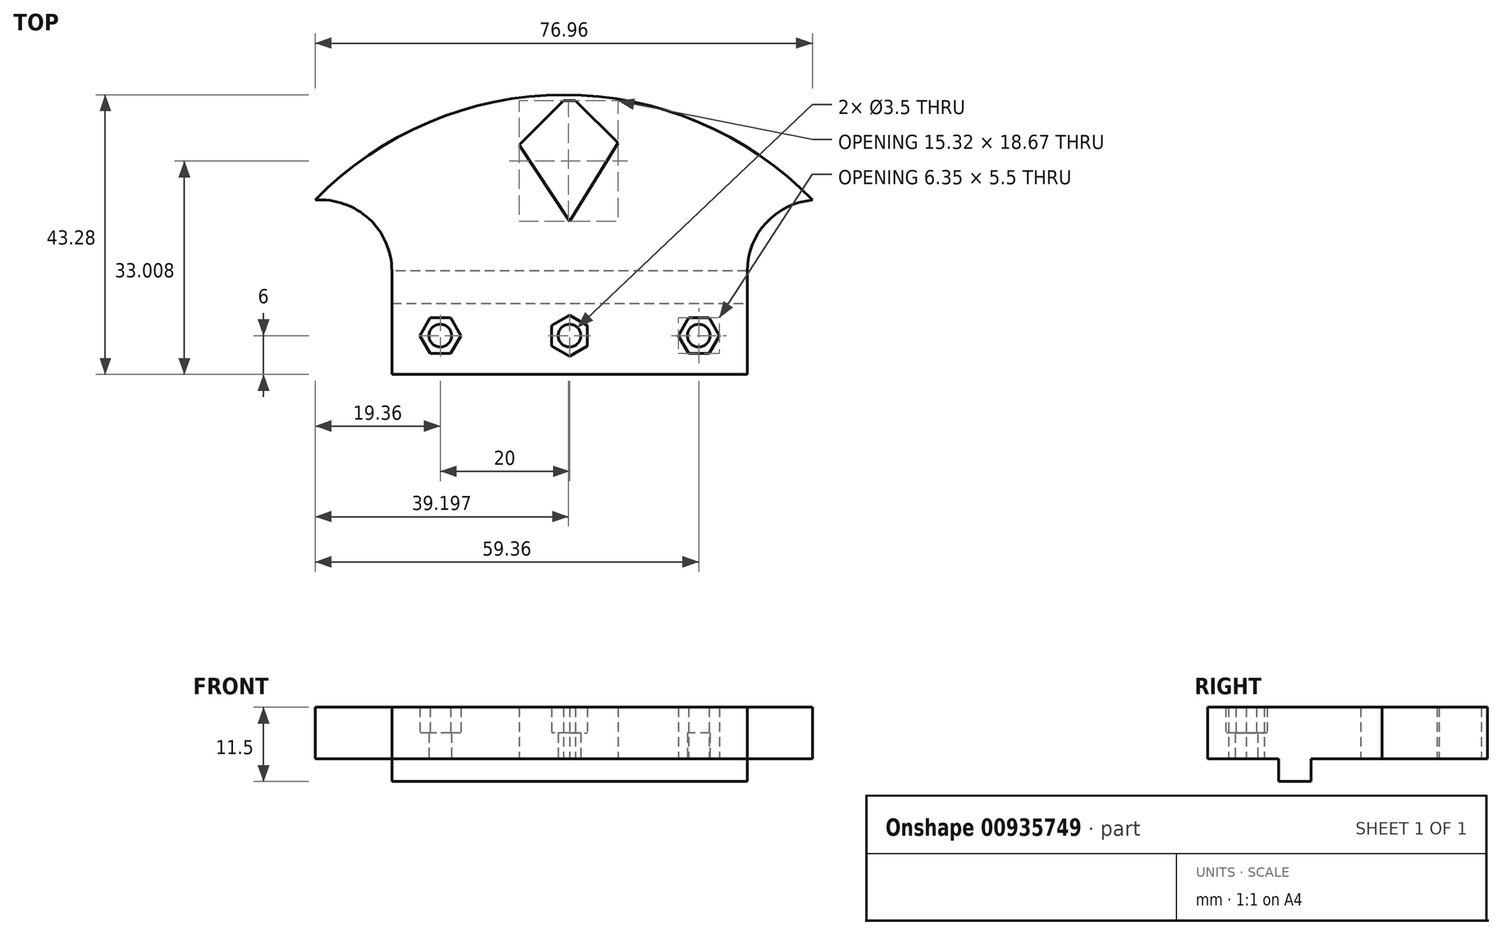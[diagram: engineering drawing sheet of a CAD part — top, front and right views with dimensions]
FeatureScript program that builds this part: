
annotation { "Feature Type Name" : "Feature", "Feature Type Description" : "" }
export const myFeature = defineFeature(function(context is Context, id is Id, definition is map)
    precondition{}
    {
        {
            var Q0;
            Q0=qCreatedBy(makeId("Top.planeOp"),FACE);
            var sketch = newSketch(context, id + "F0", { "sketchPlane" : qUnion([Q0])});
            skLineSegment(sketch, "E0.bottom", {"start": v(27.5, 8) * mm, "end": v(-27.5, 8) * mm});
            skLineSegment(sketch, "E0.top", {"start": v(27.5, -8) * mm, "end": v(-27.5, -8) * mm});
            skLineSegment(sketch, "E0.left", {"start": v(27.5, 8) * mm, "end": v(27.5, -8) * mm});
            skLineSegment(sketch, "E0.right", {"start": v(-27.5, 8) * mm, "end": v(-27.5, -8) * mm});
            skPoint(sketch, "E0.middle", {"position": v(0, 0) * mm});
            skLineSegment(sketch, "E1", {"start": v(-27.5, 3) * mm, "end": v(27.5, 3) * mm});
            skCircle(sketch, "E2.cCircle", {"center": v(0, -2) * mm, "radius": 2.75 * mm, "construction": true});
            skLineSegment(sketch, "E2.0", {"start": v(2.75, -0.41) * mm, "end": v(2.75, -3.59) * mm});
            skLineSegment(sketch, "E2.1", {"start": v(2.75, -3.59) * mm, "end": v(0, -5.18) * mm});
            skLineSegment(sketch, "E2.2", {"start": v(0, -5.18) * mm, "end": v(-2.75, -3.59) * mm});
            skLineSegment(sketch, "E2.3", {"start": v(-2.75, -3.59) * mm, "end": v(-2.75, -0.41) * mm});
            skLineSegment(sketch, "E2.4", {"start": v(-2.75, -0.41) * mm, "end": v(0, 1.18) * mm});
            skLineSegment(sketch, "E2.5", {"start": v(0, 1.18) * mm, "end": v(2.75, -0.41) * mm});
            skPoint(sketch, "E2.0.midPoint", {"position": v(2.75, -2) * mm});
            skCircle(sketch, "E3", {"center": v(0, -2) * mm, "radius": 1.75 * mm});
            skCircle(sketch, "E4.cCircle", {"center": v(-20, -2) * mm, "radius": 2.75 * mm, "construction": true});
            skLineSegment(sketch, "E4.0", {"start": v(-18.41, -4.75) * mm, "end": v(-21.59, -4.75) * mm});
            skLineSegment(sketch, "E4.1", {"start": v(-21.59, -4.75) * mm, "end": v(-23.18, -2) * mm});
            skLineSegment(sketch, "E4.2", {"start": v(-23.18, -2) * mm, "end": v(-21.59, 0.75) * mm});
            skLineSegment(sketch, "E4.3", {"start": v(-21.59, 0.75) * mm, "end": v(-18.41, 0.75) * mm});
            skLineSegment(sketch, "E4.4", {"start": v(-18.41, 0.75) * mm, "end": v(-16.82, -2) * mm});
            skLineSegment(sketch, "E4.5", {"start": v(-16.82, -2) * mm, "end": v(-18.41, -4.75) * mm});
            skPoint(sketch, "E4.0.midPoint", {"position": v(-20, -4.75) * mm});
            skCircle(sketch, "E5", {"center": v(-20, -2) * mm, "radius": 1.75 * mm});
            skLineSegment(sketch, "E6.MirrorCS", {"start": v(16.82, -2) * mm, "end": v(18.41, -4.75) * mm});
            skCircle(sketch, "E7.MirrorC", {"center": v(20, -2) * mm, "radius": 1.75 * mm});
            skPoint(sketch, "E8.MirrorP", {"position": v(20, -4.75) * mm});
            skLineSegment(sketch, "E9.MirrorCS", {"start": v(18.41, -4.75) * mm, "end": v(21.59, -4.75) * mm});
            skLineSegment(sketch, "E10.MirrorCS", {"start": v(21.59, 0.75) * mm, "end": v(18.41, 0.75) * mm});
            skCircle(sketch, "E11.MirrorC", {"center": v(20, -2) * mm, "radius": 2.75 * mm, "construction": true});
            skLineSegment(sketch, "E12.MirrorCS", {"start": v(18.41, 0.75) * mm, "end": v(16.82, -2) * mm});
            skLineSegment(sketch, "E13.MirrorCS", {"start": v(21.59, -4.75) * mm, "end": v(23.18, -2) * mm});
            skLineSegment(sketch, "E14.MirrorCS", {"start": v(23.18, -2) * mm, "end": v(21.59, 0.75) * mm});
            skArc(sketch, "E15", {"start": v(-27.5, 8) * mm, "mid": v(-31.03, 16.08) * mm, "end": v(-39.36, 18.98) * mm});
            skArc(sketch, "E16", {"start": v(37.6, 18.98) * mm, "mid": v(30.4, 15.46) * mm, "end": v(27.5, 8) * mm});
            skArc(sketch, "E17", {"start": v(37.6, 18.98) * mm, "mid": v(-0.88, 35.28) * mm, "end": v(-39.36, 18.98) * mm});
            skLineSegment(sketch, "E18", {"start": v(-27.5, 8) * mm, "end": v(-0.93, 34.34) * mm});
            skLineSegment(sketch, "E19", {"start": v(0.93, 34.34) * mm, "end": v(27.5, 8) * mm});
            skLineSegment(sketch, "E20", {"start": v(-7.82, 27.51) * mm, "end": v(0, 15.67) * mm});
            skLineSegment(sketch, "E21", {"start": v(0, 15.67) * mm, "end": v(7.5, 27.83) * mm});
            skLineSegment(sketch, "E22", {"start": v(-0.93, 34.34) * mm, "end": v(0.93, 34.34) * mm});
            skPoint(sketch, "E23.orphan", {"position": v(0, 35.27) * mm});
            skSolve(sketch);
        }
        {
            var Q0;
            {var subQ0=sQuery(id+"F0.wireOp",EDGE,"E0.top");Q0=makeQuery(id+"F0.imprint","IMPRINT",FACE,{"disambiguationData":[TD([[makeQuery(id+"F0.imprint","IMPRINT",EDGE,{"derivedFrom":subQ0}),-1.0]])]});}
            var Q1;
            {var subQ0=sQuery(id+"F0.wireOp",EDGE,"E0.bottom");Q1=makeQuery(id+"F0.imprint","IMPRINT",FACE,{"disambiguationData":[TD([[makeQuery(id+"F0.imprint","IMPRINT",EDGE,{"derivedFrom":subQ0}),1.0]])]});}
            var Q2;
            {var subQ2=sQuery(id+"F0.wireOp",EDGE,"E0.bottom");Q2=makeQuery(id+"F0.imprint","IMPRINT",FACE,{"disambiguationData":[TD([[makeQuery(id+"F0.imprint","IMPRINT",EDGE,{"derivedFrom":subQ2}),-1.0]])]});}
            var Q3;
            {var subQ0=sQuery(id+"F0.wireOp",EDGE,"E16");Q3=makeQuery(id+"F0.imprint","IMPRINT",FACE,{"disambiguationData":[TD([[makeQuery(id+"F0.imprint","IMPRINT",EDGE,{"derivedFrom":subQ0}),-1.0]])]});}
            var Q4;
            {var subQ0=sQuery(id+"F0.wireOp",EDGE,"E15");Q4=makeQuery(id+"F0.imprint","IMPRINT",FACE,{"disambiguationData":[TD([[makeQuery(id+"F0.imprint","IMPRINT",EDGE,{"derivedFrom":subQ0}),-1.0]])]});}
            extrude(context, id + "F1", {"entities" : qUnion([Q0, Q1, Q2, Q3, Q4]), "depth" : 8 * mm, "offsetDistance" : 25 * mm});
        }
        {
            var Q0;
            Q0=makeQuery(id+"F0.imprint","IMPRINT",FACE,{"disambiguationData":[TD([[makeQuery(id+"F0.imprint","IMPRINT",EDGE,{"derivedFrom":sQuery(id+"F0.wireOp",EDGE,"E4.0")}),-1.0]])]});
            var Q1;
            Q1=makeQuery(id+"F0.imprint","IMPRINT",FACE,{"disambiguationData":[TD([[makeQuery(id+"F0.imprint","IMPRINT",EDGE,{"derivedFrom":sQuery(id+"F0.wireOp",EDGE,"E2.0")}),-1.0]])]});
            var Q2;
            Q2=makeQuery(id+"F0.imprint","IMPRINT",FACE,{"disambiguationData":[TD([[makeQuery(id+"F0.imprint","IMPRINT",EDGE,{"derivedFrom":sQuery(id+"F0.wireOp",EDGE,"E7.MirrorC")}),1.0]])]});
            extrude(context, id + "F2", {"entities" : qUnion([Q0, Q1, Q2]), "operationType" : NewBodyOperationType.ADD, "depth" : 4 * mm, "offsetDistance" : 25 * mm});
        }
        {
            var Q0;
            {var subQ0=sQuery(id+"F0.wireOp",EDGE,"E0.bottom");Q0=makeQuery(id+"F0.imprint","IMPRINT",FACE,{"disambiguationData":[TD([[makeQuery(id+"F0.imprint","IMPRINT",EDGE,{"derivedFrom":subQ0}),1.0]])]});}
            extrude(context, id + "F3", {"entities" : qUnion([Q0]), "operationType" : NewBodyOperationType.ADD, "oppositeDirection" : true, "depth" : 3.5 * mm, "offsetDistance" : 25 * mm});
        }
    });
